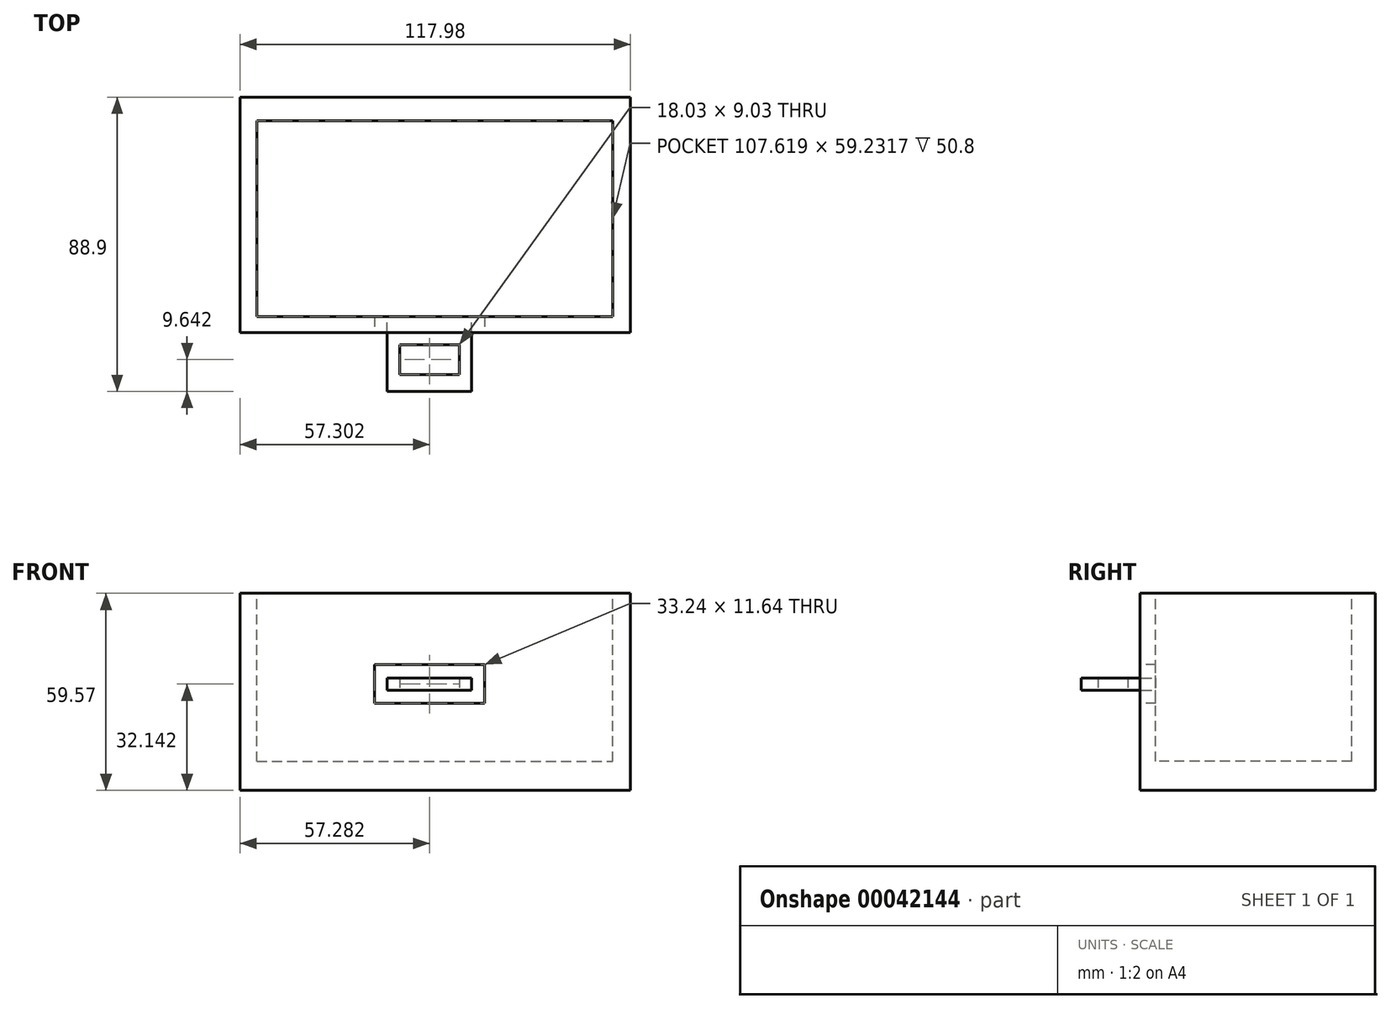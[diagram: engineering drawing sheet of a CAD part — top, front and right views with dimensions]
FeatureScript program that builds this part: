
annotation { "Feature Type Name" : "Feature", "Feature Type Description" : "" }
export const myFeature = defineFeature(function(context is Context, id is Id, definition is map)
    precondition{}
    {
        {
            var Q0;
            Q0=qCreatedBy(makeId("Front.planeOp"),FACE);
            var sketch = newSketch(context, id + "F0", { "sketchPlane" : qUnion([Q0])});
            skLineSegment(sketch, "E0.bottom", {"start": v(-57.47, 19.36) * mm, "end": v(60.5, 19.36) * mm});
            skLineSegment(sketch, "E0.top", {"start": v(-57.47, -40.2) * mm, "end": v(60.5, -40.2) * mm});
            skLineSegment(sketch, "E0.left", {"start": v(-57.47, 19.36) * mm, "end": v(-57.47, -40.2) * mm});
            skLineSegment(sketch, "E0.right", {"start": v(60.5, 19.36) * mm, "end": v(60.5, -40.2) * mm});
            skSolve(sketch);
        }
        {
            var Q0;
            Q0 = qSketchRegion(id + "F0", true);
            extrude(context, id + "F1", {"entities" : qUnion([Q0]), "depth" : 71.12 * mm});
        }
        {
            var Q0;
            Q0=makeQuery(id+"F1.opExtrude","CAP_FACE",FACE,{"disambiguationData":[OSD([sQuery(id+"F0.wireOp",EDGE,"E0.bottom"),sQuery(id+"F0.wireOp",EDGE,"E0.top"),sQuery(id+"F0.wireOp",EDGE,"E0.left"),sQuery(id+"F0.wireOp",EDGE,"E0.right")])],"isStart":false});
            var sketch = newSketch(context, id + "F2", { "sketchPlane" : qUnion([Q0])});
            skLineSegment(sketch, "E1.bottom", {"start": v(-16.8, -2.25) * mm, "end": v(16.43, -2.25) * mm});
            skLineSegment(sketch, "E1.top", {"start": v(-16.8, -13.9) * mm, "end": v(16.43, -13.9) * mm});
            skLineSegment(sketch, "E1.left", {"start": v(-16.8, -2.25) * mm, "end": v(-16.8, -13.9) * mm});
            skLineSegment(sketch, "E1.right", {"start": v(16.43, -2.25) * mm, "end": v(16.43, -13.9) * mm});
            skSolve(sketch);
        }
        {
            var Q0;
            Q0 = qSketchRegion(id + "F2", true);
            extrude(context, id + "F3", {"entities" : qUnion([Q0]), "operationType" : NewBodyOperationType.REMOVE, "oppositeDirection" : true, "depth" : 7.62 * mm});
        }
        {
            var Q0;
            Q0=makeQuery(id+"F3.boolean.opBoolean","COPY",FACE,{"derivedFrom":makeQuery(id+"F3.opExtrude","CAP_FACE",FACE,{"disambiguationData":[OSD([sQuery(id+"F2.wireOp",EDGE,"E1.bottom"),sQuery(id+"F2.wireOp",EDGE,"E1.top"),sQuery(id+"F2.wireOp",EDGE,"E1.left"),sQuery(id+"F2.wireOp",EDGE,"E1.right")])],"isStart":false})});
            var sketch = newSketch(context, id + "F4", { "sketchPlane" : qUnion([Q0])});
            skLineSegment(sketch, "E2.bottom", {"start": v(-13.05, -6.19) * mm, "end": v(12.49, -6.19) * mm});
            skLineSegment(sketch, "E2.top", {"start": v(-13.05, -9.95) * mm, "end": v(12.49, -9.95) * mm});
            skLineSegment(sketch, "E2.left", {"start": v(-13.05, -6.19) * mm, "end": v(-13.05, -9.95) * mm});
            skLineSegment(sketch, "E2.right", {"start": v(12.49, -6.19) * mm, "end": v(12.49, -9.95) * mm});
            skSolve(sketch);
        }
        {
            var Q0;
            Q0 = qSketchRegion(id + "F4", true);
            extrude(context, id + "F5", {"entities" : qUnion([Q0]), "operationType" : NewBodyOperationType.ADD, "depth" : 25.4 * mm});
        }
        {
            var Q0;
            Q0=makeQuery(id+"F5.opExtrude","SWEPT_FACE",FACE,{"disambiguationData":[OSD([sQuery(id+"F4.wireOp",EDGE,"E2.top")])]});
            var sketch = newSketch(context, id + "F6", { "sketchPlane" : qUnion([Q0])});
            skLineSegment(sketch, "E3.bottom", {"start": v(-9.18, 83.77) * mm, "end": v(8.85, 83.77) * mm});
            skLineSegment(sketch, "E3.top", {"start": v(-9.18, 74.74) * mm, "end": v(8.85, 74.74) * mm});
            skLineSegment(sketch, "E3.left", {"start": v(-9.18, 83.77) * mm, "end": v(-9.18, 74.74) * mm});
            skLineSegment(sketch, "E3.right", {"start": v(8.85, 83.77) * mm, "end": v(8.85, 74.74) * mm});
            skSolve(sketch);
        }
        {
            var Q0;
            Q0 = qSketchRegion(id + "F6", true);
            extrude(context, id + "F7", {"entities" : qUnion([Q0]), "operationType" : NewBodyOperationType.REMOVE, "oppositeDirection" : true, "depth" : 5.08 * mm});
        }
        {
            var Q0;
            Q0=makeQuery(id+"F1.opExtrude","SWEPT_FACE",FACE,{"disambiguationData":[OSD([sQuery(id+"F0.wireOp",EDGE,"E0.bottom")])]});
            var sketch = newSketch(context, id + "F8", { "sketchPlane" : qUnion([Q0])});
            skLineSegment(sketch, "E4.bottom", {"start": v(-52.38, -7.1) * mm, "end": v(55.24, -7.1) * mm});
            skLineSegment(sketch, "E4.top", {"start": v(-52.38, -66.33) * mm, "end": v(55.24, -66.33) * mm});
            skLineSegment(sketch, "E4.left", {"start": v(-52.38, -7.1) * mm, "end": v(-52.38, -66.33) * mm});
            skLineSegment(sketch, "E4.right", {"start": v(55.24, -7.1) * mm, "end": v(55.24, -66.33) * mm});
            skSolve(sketch);
        }
        {
            var Q0;
            Q0 = qSketchRegion(id + "F8", true);
            extrude(context, id + "F9", {"entities" : qUnion([Q0]), "operationType" : NewBodyOperationType.REMOVE, "oppositeDirection" : true, "depth" : 50.8 * mm});
        }
    });
